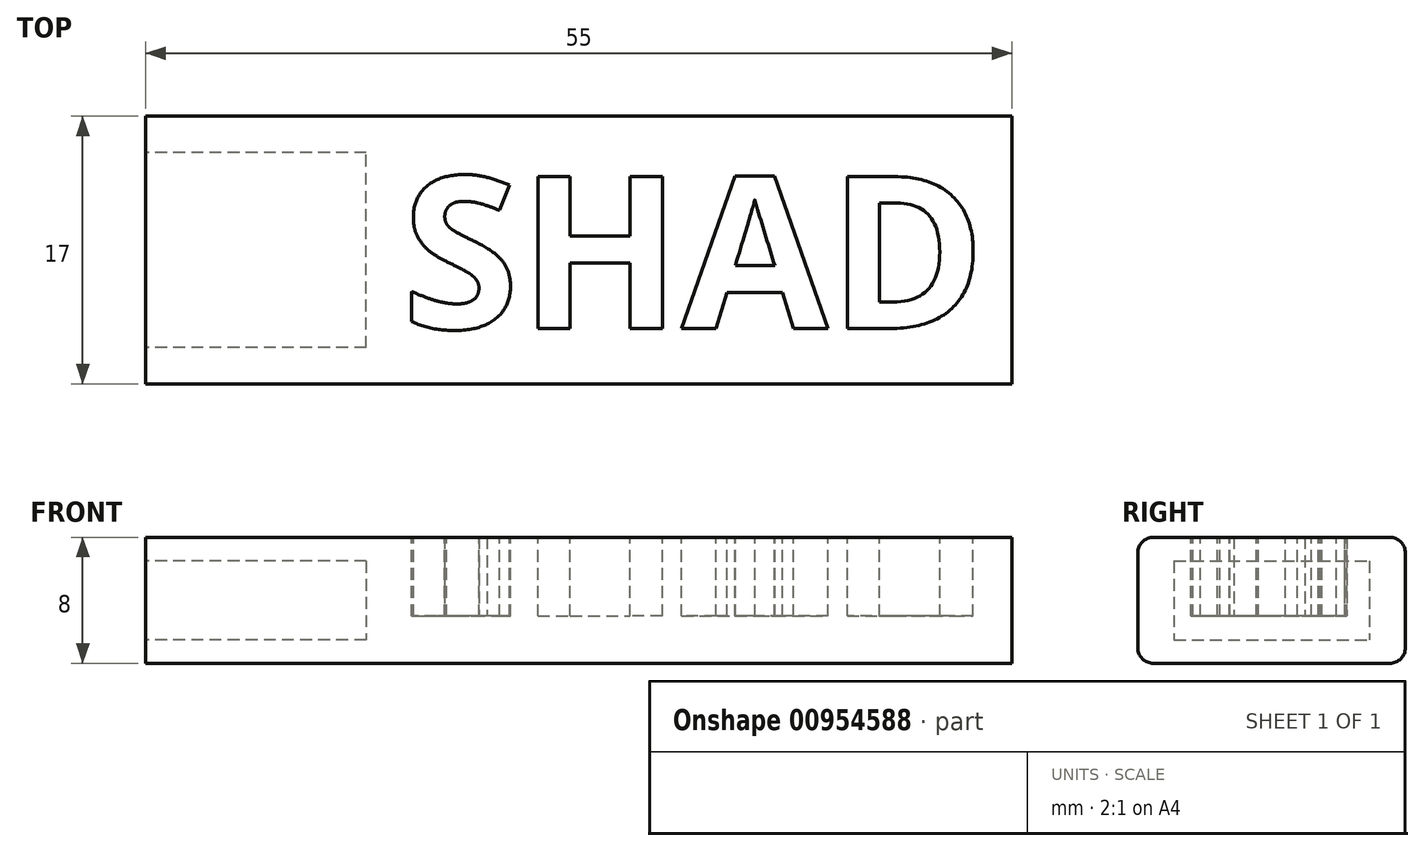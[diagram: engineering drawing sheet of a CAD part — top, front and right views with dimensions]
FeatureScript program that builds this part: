
annotation { "Feature Type Name" : "Feature", "Feature Type Description" : "" }
export const myFeature = defineFeature(function(context is Context, id is Id, definition is map)
    precondition{}
    {
        {
            var Q0;
            Q0=qCreatedBy(makeId("Front.planeOp"),FACE);
            var sketch = newSketch(context, id + "F0", { "sketchPlane" : qUnion([Q0])});
            skLineSegment(sketch, "E0.bottom", {"start": v(8.5, -4) * mm, "end": v(-8.5, -4) * mm});
            skLineSegment(sketch, "E0.top", {"start": v(8.5, 4) * mm, "end": v(-8.5, 4) * mm});
            skLineSegment(sketch, "E0.left", {"start": v(8.5, -4) * mm, "end": v(8.5, 4) * mm});
            skLineSegment(sketch, "E0.right", {"start": v(-8.5, -4) * mm, "end": v(-8.5, 4) * mm});
            skPoint(sketch, "E0.middle", {"position": v(0, 0) * mm});
            skLineSegment(sketch, "E1.bottom", {"start": v(17, 8) * mm, "end": v(-17, 8) * mm});
            skLineSegment(sketch, "E1.top", {"start": v(17, -8) * mm, "end": v(-17, -8) * mm});
            skLineSegment(sketch, "E1.left", {"start": v(17, 8) * mm, "end": v(17, -8) * mm});
            skLineSegment(sketch, "E1.right", {"start": v(-17, 8) * mm, "end": v(-17, -8) * mm});
            skSolve(sketch);
        }
        {
            var Q0;
            Q0=makeQuery(id+"F0.imprint","IMPRINT",FACE,{"disambiguationData":[TD([[makeQuery(id+"F0.imprint","IMPRINT",EDGE,{"derivedFrom":sQuery(id+"F0.wireOp",EDGE,"E0.bottom")}),-1.0]])]});
            extrude(context, id + "F1", {"entities" : qUnion([Q0]), "depth" : 55 * mm, "offsetDistance" : 25 * mm});
        }
        {
            var Q0;
            Q0=makeQuery(id+"F1.opExtrude","SWEPT_EDGE",EDGE,{"disambiguationData":[OSD([sQuery(id+"F0.wireOp",EDGE,"E0.top"),sQuery(id+"F0.wireOp",EDGE,"E0.left")])]});
            var Q1;
            Q1=makeQuery(id+"F1.opExtrude","SWEPT_EDGE",EDGE,{"disambiguationData":[OSD([sQuery(id+"F0.wireOp",EDGE,"E0.top"),sQuery(id+"F0.wireOp",EDGE,"E0.right")])]});
            var Q2;
            Q2=makeQuery(id+"F1.opExtrude","SWEPT_EDGE",EDGE,{"disambiguationData":[OSD([sQuery(id+"F0.wireOp",EDGE,"E0.bottom"),sQuery(id+"F0.wireOp",EDGE,"E0.left")])]});
            var Q3;
            Q3=makeQuery(id+"F1.opExtrude","SWEPT_EDGE",EDGE,{"disambiguationData":[OSD([sQuery(id+"F0.wireOp",EDGE,"E0.bottom"),sQuery(id+"F0.wireOp",EDGE,"E0.right")])]});
            fillet(context, id + "F2", {"entities" : qUnion([Q0, Q1, Q2, Q3]), "radius" : 1 * mm, "tangentPropagation" : true, "allowEdgeOverflow" : false});
        }
        {
            var Q0;
            Q0=makeQuery(id+"F1.opExtrude","CAP_FACE",FACE,{"disambiguationData":[OSD([sQuery(id+"F0.wireOp",EDGE,"E0.bottom"),sQuery(id+"F0.wireOp",EDGE,"E0.top"),sQuery(id+"F0.wireOp",EDGE,"E0.left"),sQuery(id+"F0.wireOp",EDGE,"E0.right")])],"isStart":true});
            var sketch = newSketch(context, id + "F3", { "sketchPlane" : qUnion([Q0])});
            skLineSegment(sketch, "E2.bottom", {"start": v(6.2, 2.5) * mm, "end": v(-6.2, 2.5) * mm});
            skLineSegment(sketch, "E2.top", {"start": v(6.2, -2.5) * mm, "end": v(-6.2, -2.5) * mm});
            skLineSegment(sketch, "E2.left", {"start": v(6.2, 2.5) * mm, "end": v(6.2, -2.5) * mm});
            skLineSegment(sketch, "E2.right", {"start": v(-6.2, 2.5) * mm, "end": v(-6.2, -2.5) * mm});
            skPoint(sketch, "E2.middle", {"position": v(0, 0) * mm});
            skSolve(sketch);
        }
        {
            var Q0;
            Q0=makeQuery(id+"F3.imprint","IMPRINT",FACE,{"disambiguationData":[TD([[makeQuery(id+"F3.imprint","IMPRINT",EDGE,{"derivedFrom":sQuery(id+"F3.wireOp",EDGE,"E2.bottom")}),1.0]])]});
            extrude(context, id + "F4", {"entities" : qUnion([Q0]), "operationType" : NewBodyOperationType.REMOVE, "oppositeDirection" : true, "depth" : 14 * mm, "offsetDistance" : 25 * mm});
        }
        {
            var Q0;
            Q0=makeQuery(id+"F1.opExtrude","SWEPT_BODY",BODY,{"disambiguationData":[OSD([sQuery(id+"F0.wireOp",EDGE,"E0.bottom"),sQuery(id+"F0.wireOp",EDGE,"E0.top"),sQuery(id+"F0.wireOp",EDGE,"E0.left"),sQuery(id+"F0.wireOp",EDGE,"E0.right")])]});
            var Q1;
            Q1=makeQuery(id+"F1.opExtrude","CAP_EDGE",EDGE,{"disambiguationData":[OSD([sQuery(id+"F0.wireOp",EDGE,"E0.left")])],"isStart":true});
            transform(context, id + "F5", {"entities" : qUnion([Q0]), "transformType" : TransformType.ROTATION, "transformAxis" : qUnion([Q1]), "angle" : 90 * degree, "makeCopy" : false});
        }
        {
            var Q0;
            Q0=makeQuery(id+"F1.opExtrude","SWEPT_FACE",FACE,{"disambiguationData":[OSD([sQuery(id+"F0.wireOp",EDGE,"E0.top")])]});
            var sketch = newSketch(context, id + "F6", { "sketchPlane" : qUnion([Q0])});
            skText(sketch, "E3", { "text": "SHAD", "fontName": "OpenSans-Bold.ttf"});
            const initialGuessF6  = {"E3": [0.02476, -0.01348, 1, 0, 0.00972]};
            skSetInitialGuess(sketch, initialGuessF6);
            skSolve(sketch);
        }
        {
            var Q0;
            Q0 = qSketchRegion(id + "F6", true);
            extrude(context, id + "F7", {"entities" : qUnion([Q0]), "operationType" : NewBodyOperationType.REMOVE, "oppositeDirection" : true, "depth" : 5 * mm, "offsetDistance" : 25 * mm});
        }
    });
